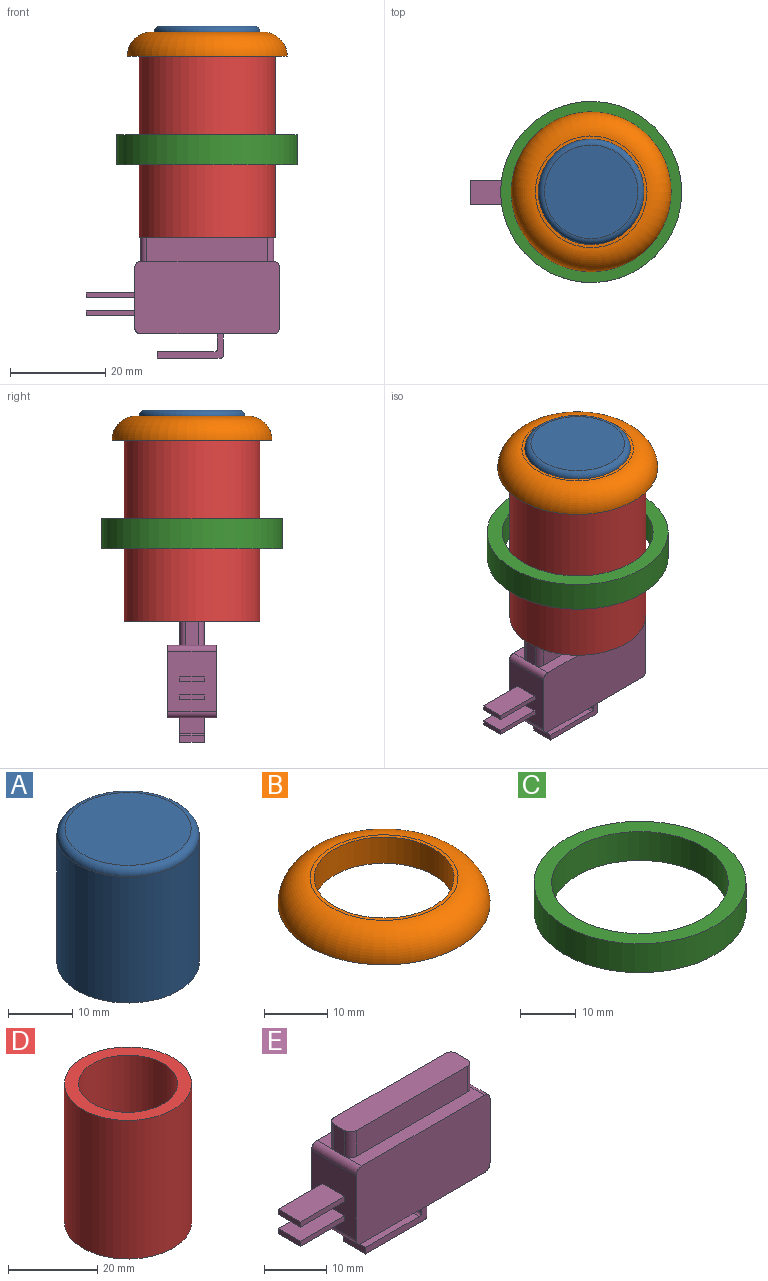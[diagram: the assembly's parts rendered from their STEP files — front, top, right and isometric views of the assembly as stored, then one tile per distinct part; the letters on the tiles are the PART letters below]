
ASSEMBLY  parts=5 mates=4
PART A: 4 faces, bbox 24.1x24.1x25.4 mm
  f0: cylinder r=11.11mm len=24.13mm, axis (0,0,-1), area 1684.8mm2, adj f2,f3
  f1: plane 19.69x19.69mm, normal (0,0,1), area 304.3mm2, adj f3
  f2: plane 22.23x22.23mm, normal (0,0,-1), area 387.9mm2, adj f0
  f3: torus R=9.84mm, axis (0,0,1), area 133.5mm2, adj f0,f1
PART B: 4 faces, bbox 36.4x36.4x5.1 mm
  f0: cylinder r=11.11mm len=22.23mm, axis (0,0,-1), area 354.7mm2, adj f1,f2
  f1: plane 23.5x23.5mm, normal (0,0,1), area 45.6mm2, adj f0,f3
  f2: plane 33.66x33.66mm, normal (0,0,-1), area 501.6mm2, adj f0,f3
  f3: torus R=11.75mm, axis (0,0,1), area 751.1mm2, adj f1,f2
PART C: 4 faces, bbox 38.1x38.1x6.4 mm
  f0: cylinder r=15.88mm len=31.75mm, axis (0,0,-1), area 633.4mm2, adj f1,f3
  f1: plane 38.1x38.1mm, normal (0,0,1), area 348.4mm2, adj f0,f2
  f2: cylinder r=19.05mm len=38.1mm, axis (0,0,-1), area 760.1mm2, adj f1,f3
  f3: plane 38.1x38.1mm, normal (0,0,-1), area 348.4mm2, adj f0,f2
PART D: 4 faces, bbox 28.6x28.6x38.1 mm
  f0: cylinder r=11.11mm len=38.1mm, axis (0,0,1), area 2660.2mm2, adj f2,f3
  f1: cylinder r=14.29mm len=38.1mm, axis (0,0,1), area 3420.3mm2, adj f2,f3
  f2: plane 28.58x28.58mm, normal (0,0,-1), area 253.4mm2, adj f0,f1
  f3: plane 28.58x28.58mm, normal (0,0,1), area 253.4mm2, adj f0,f1
PART E: 39 faces, bbox 40.6x10.2x25.4 mm
  f0: plane 27.94x3.81mm, normal (0,0,1), area 71.7mm2, adj f5,f26,f27,f32,f36,f37
  f1: plane 5.08x3.3mm, normal (-1,0,0), area 16.8mm2, adj f6,f18,f19,f24
  f2: plane 12.7x10.16mm, normal (-1,0,0), area 118.7mm2, adj f4,f5,f8,f9,f10,f11,f13,f14
  f3: plane 12.7x10.16mm, normal (1,0,0), area 129mm2, adj f4,f5,f27,f29
  f4: plane 30.48x15.24mm, normal (0,1,0), area 463.1mm2, adj f2,f3,f6,f7,f26,f27,f28,f29
  f5: plane 30.48x15.24mm, normal (0,-1,0), area 463.1mm2, adj f0,f2,f3,f6,f26,f27,f28,f29
  f6: plane 27.94x10.16mm, normal (0,0,-1), area 277.4mm2, adj f1,f4,f5,f18,f19,f20,f28,f29
  f7: plane 27.94x3.81mm, normal (0,0,1), area 71.7mm2, adj f4,f26,f27,f30,f35,f38
  f8: plane 10.16x5.08mm, normal (0,0,1), area 51.6mm2, adj f2,f9,f11,f12
  f9: plane 10.16x1.02mm, normal (0,1,0), area 10.3mm2, adj f2,f8,f10,f12
  f10: plane 10.16x5.08mm, normal (0,0,-1), area 51.6mm2, adj f2,f9,f11,f12
  f11: plane 10.16x1.02mm, normal (0,-1,0), area 10.3mm2, adj f2,f8,f10,f12
  f12: plane 5.08x1.02mm, normal (-1,0,0), area 5.2mm2, adj f8,f9,f10,f11
  f13: plane 10.16x5.08mm, normal (0,0,1), area 51.6mm2, adj f2,f14,f16,f17
  f14: plane 10.16x1.02mm, normal (0,1,0), area 10.3mm2, adj f2,f13,f15,f17
  f15: plane 10.16x5.08mm, normal (0,0,-1), area 51.6mm2, adj f2,f14,f16,f17
  f16: plane 10.16x1.02mm, normal (0,-1,0), area 10.3mm2, adj f2,f13,f15,f17
  f17: plane 5.08x1.02mm, normal (-1,0,0), area 5.2mm2, adj f13,f14,f15,f16
  f18: plane 13.97x5.08mm, normal (0,-1,0), area 22.6mm2, adj f1,f6,f20,f21,f22,f23,f24,f25
  f19: plane 13.97x5.08mm, normal (0,1,0), area 22.6mm2, adj f1,f6,f20,f21,f22,f23,f24,f25
  f20: plane 5.08x4.57mm, normal (1,0,0), area 23.2mm2, adj f6,f18,f19,f25
  f21: plane 13.46x5.08mm, normal (0,0,-1), area 68.4mm2, adj f18,f19,f23,f25
  f22: plane 12.19x5.08mm, normal (0,0,1), area 61.9mm2, adj f18,f19,f23,f24
  f23: plane 5.08x1.27mm, normal (-1,0,0), area 6.5mm2, adj f18,f19,f21,f22
  f24: cylinder r=0.51mm len=5.08mm, axis (0,-1,0), area 4.1mm2, adj f1,f18,f19,f22
  f25: cylinder r=0.51mm len=5.08mm, axis (0,1,0), area 4.1mm2, adj f18,f19,f20,f21
  f26: cylinder r=1.27mm len=10.16mm, axis (0,-1,0), area 20.3mm2, adj f0,f2,f4,f5,f7,f31
  f27: cylinder r=1.27mm len=10.16mm, axis (0,1,0), area 20.3mm2, adj f0,f3,f4,f5,f7,f33
  f28: cylinder r=1.27mm len=10.16mm, axis (0,1,0), area 20.3mm2, adj f2,f4,f5,f6
  f29: cylinder r=1.27mm len=10.16mm, axis (0,-1,0), area 20.3mm2, adj f3,f4,f5,f6
  f30: plane 25.4x5.08mm, normal (0,1,0), area 129mm2, adj f7,f34,f35,f38
  f31: plane 5.08x2.54mm, normal (-1,0,0), area 12.9mm2, adj f26,f34,f35,f36
  f32: plane 25.4x5.08mm, normal (0,-1,0), area 129mm2, adj f0,f34,f36,f37
  f33: plane 5.08x2.54mm, normal (1,0,0), area 12.9mm2, adj f27,f34,f37,f38
  f34: plane 27.94x5.08mm, normal (0,0,1), area 140.6mm2, adj f30,f31,f32,f33,f35,f36,f37,f38
  f35: cylinder r=1.27mm len=5.08mm, axis (0,0,1), area 10.1mm2, adj f7,f30,f31,f34
  f36: cylinder r=1.27mm len=5.08mm, axis (0,0,-1), area 10.1mm2, adj f0,f31,f32,f34
  f37: cylinder r=1.27mm len=5.08mm, axis (0,0,-1), area 10.1mm2, adj f0,f32,f33,f34
  f38: cylinder r=1.27mm len=5.08mm, axis (0,0,1), area 10.1mm2, adj f7,f30,f33,f34
PLACE A t=(25.45,-7.5,3.41)mm
PLACE B t=(-12.03,-7.5,7.22)mm
PLACE C t=(-12.03,39.06,-15.64)mm
PLACE D t=(-55.61,-7.5,7.22)mm fixed
PLACE E t=(33.9,22.11,-35.96)mm
MATE fastened E.f34 <-> D.f0  axis (0,0,1) through (-12.03,39.06,-30.88)mm
MATE fastened D.f0 <-> B.f0  axis (0,0,1) through (-12.03,39.06,7.22)mm
MATE slider C.f0 <-> D.f0  axis (0,0,-1) through (-12.03,39.06,-15.64)mm
MATE slider A.f0 <-> B.f0  axis (0,0,-1) through (-12.03,39.06,12.3)mm
